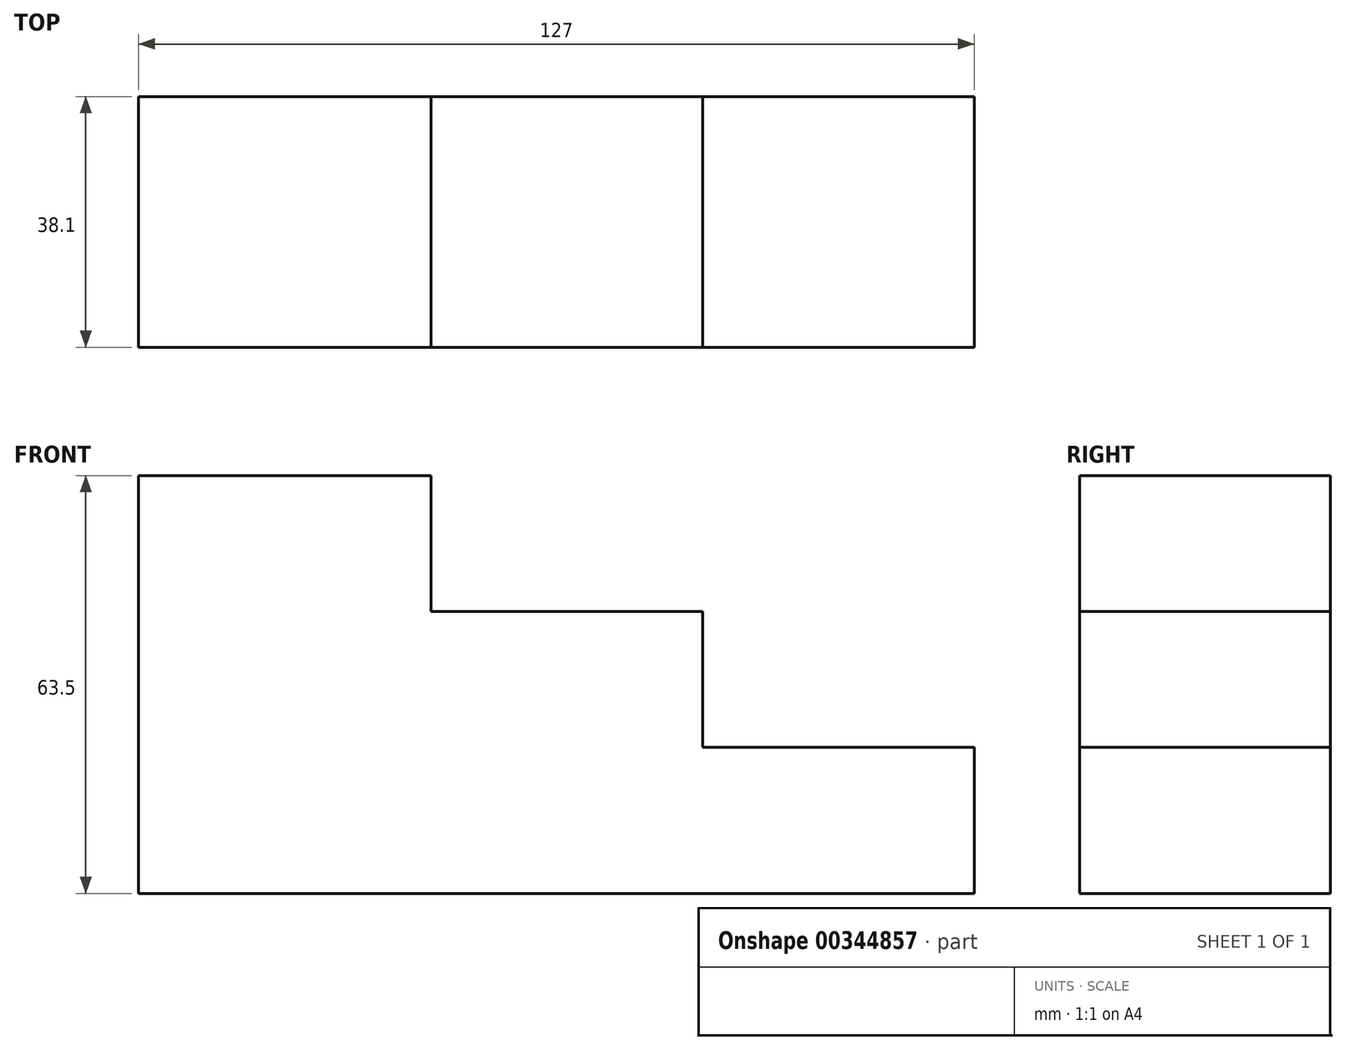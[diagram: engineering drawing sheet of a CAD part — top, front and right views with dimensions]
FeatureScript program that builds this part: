
annotation { "Feature Type Name" : "Feature", "Feature Type Description" : "" }
export const myFeature = defineFeature(function(context is Context, id is Id, definition is map)
    precondition{}
    {
        {
            var Q0;
            Q0=qCreatedBy(makeId("Front.planeOp"),FACE);
            var sketch = newSketch(context, id + "F0", { "sketchPlane" : qUnion([Q0])});
            skLineSegment(sketch, "E0.bottom", {"start": v(-19.05, 31.75) * mm, "end": v(-63.5, 31.75) * mm});
            skLineSegment(sketch, "E0.top", {"start": v(63.5, -31.75) * mm, "end": v(-63.5, -31.75) * mm});
            skLineSegment(sketch, "E0.left", {"start": v(63.5, -9.52) * mm, "end": v(63.5, -31.75) * mm});
            skLineSegment(sketch, "E0.right", {"start": v(-63.5, 31.75) * mm, "end": v(-63.5, -31.75) * mm});
            skPoint(sketch, "E0.middle", {"position": v(0, 0) * mm});
            skLineSegment(sketch, "E1.top", {"start": v(22.23, 11.11) * mm, "end": v(-19.05, 11.11) * mm});
            skLineSegment(sketch, "E1.right", {"start": v(-19.05, 31.75) * mm, "end": v(-19.05, 11.11) * mm});
            skLineSegment(sketch, "E2.top", {"start": v(63.5, -9.52) * mm, "end": v(22.23, -9.52) * mm});
            skLineSegment(sketch, "E2.right", {"start": v(22.23, 11.11) * mm, "end": v(22.23, -9.52) * mm});
            skPoint(sketch, "E3.orphan", {"position": v(63.5, 31.75) * mm});
            skSolve(sketch);
        }
        {
            var Q0;
            Q0 = qSketchRegion(id + "F0", true);
            extrude(context, id + "F1", {"entities" : qUnion([Q0]), "depth" : 38.1 * mm});
        }
    });
